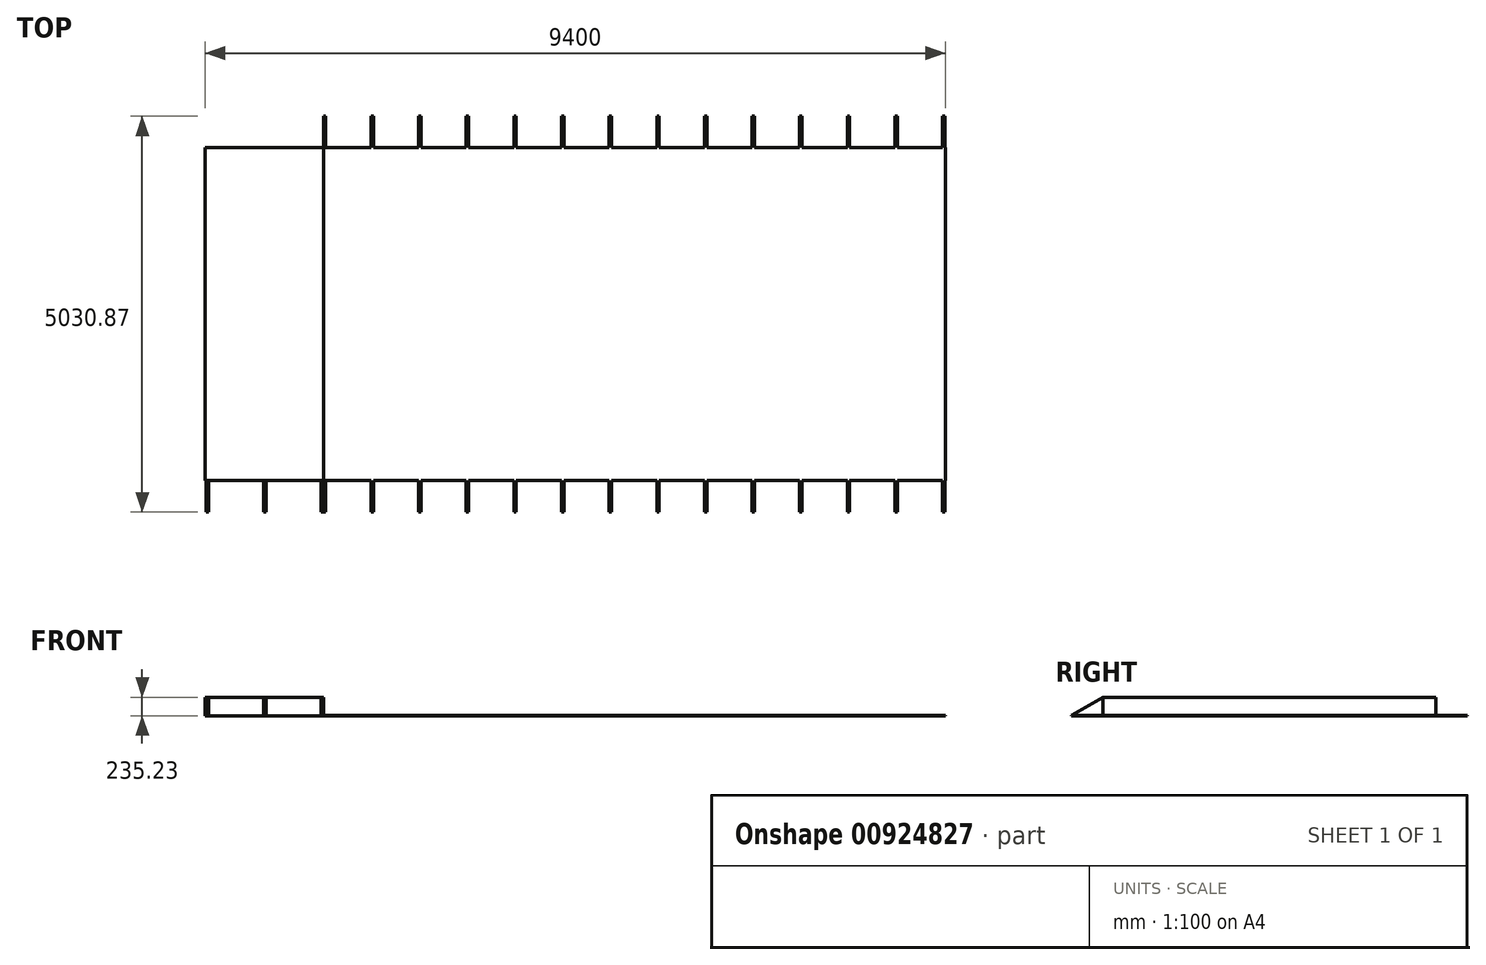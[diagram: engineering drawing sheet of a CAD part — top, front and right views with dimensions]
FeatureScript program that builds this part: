
annotation { "Feature Type Name" : "Feature", "Feature Type Description" : "" }
export const myFeature = defineFeature(function(context is Context, id is Id, definition is map)
    precondition{}
    {
        {
            var Q0;
            Q0=qCreatedBy(makeId("Top.planeOp"),FACE);
            var sketch = newSketch(context, id + "F0", { "sketchPlane" : qUnion([Q0])});
            skLineSegment(sketch, "E0.bottom", {"start": v(-1549.76, 3949.93) * mm, "end": v(-49.76, 3949.93) * mm});
            skLineSegment(sketch, "E0.top", {"start": v(-1549.76, -280.07) * mm, "end": v(-49.76, -280.07) * mm});
            skLineSegment(sketch, "E0.left", {"start": v(-1549.76, 3949.93) * mm, "end": v(-1549.76, -280.07) * mm});
            skLineSegment(sketch, "E0.right", {"start": v(-49.76, 3949.93) * mm, "end": v(-49.76, -280.07) * mm});
            skSolve(sketch);
        }
        {
            var Q0;
            Q0 = qSketchRegion(id + "F0", true);
            extrude(context, id + "F1", {"entities" : qUnion([Q0]), "depth" : 235 * mm, "offsetDistance" : 25 * mm});
        }
        {
            var Q0;
            Q0=qCreatedBy(makeId("Top.planeOp"),FACE);
            var sketch = newSketch(context, id + "F2", { "sketchPlane" : qUnion([Q0])});
            skLineSegment(sketch, "E1.bottom", {"start": v(-49.76, 3949.93) * mm, "end": v(7850.24, 3949.93) * mm});
            skLineSegment(sketch, "E1.top", {"start": v(-49.76, -280.07) * mm, "end": v(7850.24, -280.07) * mm});
            skLineSegment(sketch, "E1.left", {"start": v(-49.76, 3949.93) * mm, "end": v(-49.76, -280.07) * mm});
            skLineSegment(sketch, "E1.right", {"start": v(7850.24, 3949.93) * mm, "end": v(7850.24, -280.07) * mm});
            skSolve(sketch);
        }
        {
            var Q0;
            Q0 = qSketchRegion(id + "F2", true);
            extrude(context, id + "F3", {"entities" : qUnion([Q0]), "operationType" : NewBodyOperationType.ADD, "depth" : 2 * mm, "offsetDistance" : 25 * mm});
        }
        {
            var Q0;
            Q0=qCreatedBy(makeId("Top.planeOp"),FACE);
            var sketch = newSketch(context, id + "F4", { "sketchPlane" : qUnion([Q0])});
            skLineSegment(sketch, "E2.bottom", {"start": v(-49.76, 3949.93) * mm, "end": v(-19.76, 3949.93) * mm});
            skLineSegment(sketch, "E2.top", {"start": v(-49.76, 4349.93) * mm, "end": v(-19.76, 4349.93) * mm});
            skLineSegment(sketch, "E2.left", {"start": v(-49.76, 3949.93) * mm, "end": v(-49.76, 4349.93) * mm});
            skLineSegment(sketch, "E2.right", {"start": v(-19.76, 3949.93) * mm, "end": v(-19.76, 4349.93) * mm});
            skLineSegment(sketch, "E3", {"start": v(-2578.41, 1834.93) * mm, "end": v(9078.03, 1834.93) * mm, "construction": true});
            skLineSegment(sketch, "E4.1.0.0", {"start": v(585.24, 3949.93) * mm, "end": v(585.24, 4349.93) * mm});
            skLineSegment(sketch, "E4.1.0.1", {"start": v(555.24, 4349.93) * mm, "end": v(585.24, 4349.93) * mm});
            skLineSegment(sketch, "E4.1.0.2", {"start": v(555.24, 3949.93) * mm, "end": v(555.24, 4349.93) * mm});
            skLineSegment(sketch, "E4.1.0.3", {"start": v(555.24, 3949.93) * mm, "end": v(585.24, 3949.93) * mm});
            skLineSegment(sketch, "E4.2.0.0", {"start": v(1190.24, 3949.93) * mm, "end": v(1190.24, 4349.93) * mm});
            skLineSegment(sketch, "E4.2.0.1", {"start": v(1160.24, 4349.93) * mm, "end": v(1190.24, 4349.93) * mm});
            skLineSegment(sketch, "E4.2.0.2", {"start": v(1160.24, 3949.93) * mm, "end": v(1160.24, 4349.93) * mm});
            skLineSegment(sketch, "E4.2.0.3", {"start": v(1160.24, 3949.93) * mm, "end": v(1190.24, 3949.93) * mm});
            skLineSegment(sketch, "E4.3.0.0", {"start": v(1795.24, 3949.93) * mm, "end": v(1795.24, 4349.93) * mm});
            skLineSegment(sketch, "E4.3.0.1", {"start": v(1765.24, 4349.93) * mm, "end": v(1795.24, 4349.93) * mm});
            skLineSegment(sketch, "E4.3.0.2", {"start": v(1765.24, 3949.93) * mm, "end": v(1765.24, 4349.93) * mm});
            skLineSegment(sketch, "E4.3.0.3", {"start": v(1765.24, 3949.93) * mm, "end": v(1795.24, 3949.93) * mm});
            skLineSegment(sketch, "E4.4.0.0", {"start": v(2400.24, 3949.93) * mm, "end": v(2400.24, 4349.93) * mm});
            skLineSegment(sketch, "E4.4.0.1", {"start": v(2370.24, 4349.93) * mm, "end": v(2400.24, 4349.93) * mm});
            skLineSegment(sketch, "E4.4.0.2", {"start": v(2370.24, 3949.93) * mm, "end": v(2370.24, 4349.93) * mm});
            skLineSegment(sketch, "E4.4.0.3", {"start": v(2370.24, 3949.93) * mm, "end": v(2400.24, 3949.93) * mm});
            skLineSegment(sketch, "E4.5.0.0", {"start": v(3005.24, 3949.93) * mm, "end": v(3005.24, 4349.93) * mm});
            skLineSegment(sketch, "E4.5.0.1", {"start": v(2975.24, 4349.93) * mm, "end": v(3005.24, 4349.93) * mm});
            skLineSegment(sketch, "E4.5.0.2", {"start": v(2975.24, 3949.93) * mm, "end": v(2975.24, 4349.93) * mm});
            skLineSegment(sketch, "E4.5.0.3", {"start": v(2975.24, 3949.93) * mm, "end": v(3005.24, 3949.93) * mm});
            skLineSegment(sketch, "E4.6.0.0", {"start": v(3610.24, 3949.93) * mm, "end": v(3610.24, 4349.93) * mm});
            skLineSegment(sketch, "E4.6.0.1", {"start": v(3580.24, 4349.93) * mm, "end": v(3610.24, 4349.93) * mm});
            skLineSegment(sketch, "E4.6.0.2", {"start": v(3580.24, 3949.93) * mm, "end": v(3580.24, 4349.93) * mm});
            skLineSegment(sketch, "E4.6.0.3", {"start": v(3580.24, 3949.93) * mm, "end": v(3610.24, 3949.93) * mm});
            skLineSegment(sketch, "E4.7.0.0", {"start": v(4215.24, 3949.93) * mm, "end": v(4215.24, 4349.93) * mm});
            skLineSegment(sketch, "E4.7.0.1", {"start": v(4185.24, 4349.93) * mm, "end": v(4215.24, 4349.93) * mm});
            skLineSegment(sketch, "E4.7.0.2", {"start": v(4185.24, 3949.93) * mm, "end": v(4185.24, 4349.93) * mm});
            skLineSegment(sketch, "E4.7.0.3", {"start": v(4185.24, 3949.93) * mm, "end": v(4215.24, 3949.93) * mm});
            skLineSegment(sketch, "E4.8.0.0", {"start": v(4820.24, 3949.93) * mm, "end": v(4820.24, 4349.93) * mm});
            skLineSegment(sketch, "E4.8.0.1", {"start": v(4790.24, 4349.93) * mm, "end": v(4820.24, 4349.93) * mm});
            skLineSegment(sketch, "E4.8.0.2", {"start": v(4790.24, 3949.93) * mm, "end": v(4790.24, 4349.93) * mm});
            skLineSegment(sketch, "E4.8.0.3", {"start": v(4790.24, 3949.93) * mm, "end": v(4820.24, 3949.93) * mm});
            skLineSegment(sketch, "E4.9.0.0", {"start": v(5425.24, 3949.93) * mm, "end": v(5425.24, 4349.93) * mm});
            skLineSegment(sketch, "E4.9.0.1", {"start": v(5395.24, 4349.93) * mm, "end": v(5425.24, 4349.93) * mm});
            skLineSegment(sketch, "E4.9.0.2", {"start": v(5395.24, 3949.93) * mm, "end": v(5395.24, 4349.93) * mm});
            skLineSegment(sketch, "E4.9.0.3", {"start": v(5395.24, 3949.93) * mm, "end": v(5425.24, 3949.93) * mm});
            skLineSegment(sketch, "E4.10.0.0", {"start": v(6030.24, 3949.93) * mm, "end": v(6030.24, 4349.93) * mm});
            skLineSegment(sketch, "E4.10.0.1", {"start": v(6000.24, 4349.93) * mm, "end": v(6030.24, 4349.93) * mm});
            skLineSegment(sketch, "E4.10.0.2", {"start": v(6000.24, 3949.93) * mm, "end": v(6000.24, 4349.93) * mm});
            skLineSegment(sketch, "E4.10.0.3", {"start": v(6000.24, 3949.93) * mm, "end": v(6030.24, 3949.93) * mm});
            skLineSegment(sketch, "E4.11.0.0", {"start": v(6635.24, 3949.93) * mm, "end": v(6635.24, 4349.93) * mm});
            skLineSegment(sketch, "E4.11.0.1", {"start": v(6605.24, 4349.93) * mm, "end": v(6635.24, 4349.93) * mm});
            skLineSegment(sketch, "E4.11.0.2", {"start": v(6605.24, 3949.93) * mm, "end": v(6605.24, 4349.93) * mm});
            skLineSegment(sketch, "E4.11.0.3", {"start": v(6605.24, 3949.93) * mm, "end": v(6635.24, 3949.93) * mm});
            skLineSegment(sketch, "E4.12.0.0", {"start": v(7240.24, 3949.93) * mm, "end": v(7240.24, 4349.93) * mm});
            skLineSegment(sketch, "E4.12.0.1", {"start": v(7210.24, 4349.93) * mm, "end": v(7240.24, 4349.93) * mm});
            skLineSegment(sketch, "E4.12.0.2", {"start": v(7210.24, 3949.93) * mm, "end": v(7210.24, 4349.93) * mm});
            skLineSegment(sketch, "E4.12.0.3", {"start": v(7210.24, 3949.93) * mm, "end": v(7240.24, 3949.93) * mm});
            skLineSegment(sketch, "E4.13.0.0", {"start": v(7845.24, 3949.93) * mm, "end": v(7845.24, 4349.93) * mm});
            skLineSegment(sketch, "E4.13.0.1", {"start": v(7815.24, 4349.93) * mm, "end": v(7845.24, 4349.93) * mm});
            skLineSegment(sketch, "E4.13.0.2", {"start": v(7815.24, 3949.93) * mm, "end": v(7815.24, 4349.93) * mm});
            skLineSegment(sketch, "E4.13.0.3", {"start": v(7815.24, 3949.93) * mm, "end": v(7845.24, 3949.93) * mm});
            skLineSegment(sketch, "E4.direction1", {"start": v(-19.76, 3949.93) * mm, "end": v(585.24, 3949.93) * mm, "construction": true});
            skLineSegment(sketch, "E5.MirrorCS", {"start": v(-49.76, -680.07) * mm, "end": v(-19.76, -680.07) * mm});
            skLineSegment(sketch, "E6.MirrorCS", {"start": v(-19.76, -280.07) * mm, "end": v(-19.76, -680.07) * mm});
            skLineSegment(sketch, "E7.MirrorCS", {"start": v(-49.76, -280.07) * mm, "end": v(-49.76, -680.07) * mm});
            skLineSegment(sketch, "E8.MirrorCS", {"start": v(-49.76, -280.07) * mm, "end": v(-19.76, -280.07) * mm});
            skLineSegment(sketch, "E9.MirrorCS", {"start": v(555.24, -280.07) * mm, "end": v(585.24, -280.07) * mm});
            skLineSegment(sketch, "E10.MirrorCS", {"start": v(1765.24, -680.07) * mm, "end": v(1795.24, -680.07) * mm});
            skLineSegment(sketch, "E11.MirrorCS", {"start": v(7210.24, -280.07) * mm, "end": v(7240.24, -280.07) * mm});
            skLineSegment(sketch, "E12.MirrorCS", {"start": v(4790.24, -680.07) * mm, "end": v(4820.24, -680.07) * mm});
            skLineSegment(sketch, "E13.MirrorCS", {"start": v(3580.24, -280.07) * mm, "end": v(3610.24, -280.07) * mm});
            skLineSegment(sketch, "E14.MirrorCS", {"start": v(2370.24, -280.07) * mm, "end": v(2400.24, -280.07) * mm});
            skLineSegment(sketch, "E15.MirrorCS", {"start": v(5395.24, -280.07) * mm, "end": v(5425.24, -280.07) * mm});
            skLineSegment(sketch, "E16.MirrorCS", {"start": v(7815.24, -280.07) * mm, "end": v(7845.24, -280.07) * mm});
            skLineSegment(sketch, "E17.MirrorCS", {"start": v(6605.24, -280.07) * mm, "end": v(6635.24, -280.07) * mm});
            skLineSegment(sketch, "E18.MirrorCS", {"start": v(6000.24, -680.07) * mm, "end": v(6030.24, -680.07) * mm});
            skLineSegment(sketch, "E19.MirrorCS", {"start": v(555.24, -680.07) * mm, "end": v(585.24, -680.07) * mm});
            skLineSegment(sketch, "E20.MirrorCS", {"start": v(1765.24, -280.07) * mm, "end": v(1795.24, -280.07) * mm});
            skLineSegment(sketch, "E21.MirrorCS", {"start": v(2370.24, -680.07) * mm, "end": v(2400.24, -680.07) * mm});
            skLineSegment(sketch, "E22.MirrorCS", {"start": v(2975.24, -280.07) * mm, "end": v(3005.24, -280.07) * mm});
            skLineSegment(sketch, "E23.MirrorCS", {"start": v(7210.24, -680.07) * mm, "end": v(7240.24, -680.07) * mm});
            skLineSegment(sketch, "E24.MirrorCS", {"start": v(2975.24, -680.07) * mm, "end": v(3005.24, -680.07) * mm});
            skLineSegment(sketch, "E25.MirrorCS", {"start": v(4185.24, -680.07) * mm, "end": v(4215.24, -680.07) * mm});
            skLineSegment(sketch, "E26.MirrorCS", {"start": v(3580.24, -680.07) * mm, "end": v(3610.24, -680.07) * mm});
            skLineSegment(sketch, "E27.MirrorCS", {"start": v(7815.24, -680.07) * mm, "end": v(7845.24, -680.07) * mm});
            skLineSegment(sketch, "E28.MirrorCS", {"start": v(4790.24, -280.07) * mm, "end": v(4820.24, -280.07) * mm});
            skLineSegment(sketch, "E29.MirrorCS", {"start": v(4185.24, -280.07) * mm, "end": v(4215.24, -280.07) * mm});
            skLineSegment(sketch, "E30.MirrorCS", {"start": v(5395.24, -680.07) * mm, "end": v(5425.24, -680.07) * mm});
            skLineSegment(sketch, "E31.MirrorCS", {"start": v(6000.24, -280.07) * mm, "end": v(6030.24, -280.07) * mm});
            skLineSegment(sketch, "E32.MirrorCS", {"start": v(1160.24, -680.07) * mm, "end": v(1190.24, -680.07) * mm});
            skLineSegment(sketch, "E33.MirrorCS", {"start": v(1160.24, -280.07) * mm, "end": v(1190.24, -280.07) * mm});
            skLineSegment(sketch, "E34.MirrorCS", {"start": v(6605.24, -680.07) * mm, "end": v(6635.24, -680.07) * mm});
            skLineSegment(sketch, "E35.MirrorCS", {"start": v(585.24, -280.07) * mm, "end": v(585.24, -680.07) * mm});
            skLineSegment(sketch, "E36.MirrorCS", {"start": v(1795.24, -280.07) * mm, "end": v(1795.24, -680.07) * mm});
            skLineSegment(sketch, "E37.MirrorCS", {"start": v(6000.24, -280.07) * mm, "end": v(6000.24, -680.07) * mm});
            skLineSegment(sketch, "E38.MirrorCS", {"start": v(4790.24, -280.07) * mm, "end": v(4790.24, -680.07) * mm});
            skLineSegment(sketch, "E39.MirrorCS", {"start": v(4820.24, -280.07) * mm, "end": v(4820.24, -680.07) * mm});
            skLineSegment(sketch, "E40.MirrorCS", {"start": v(7210.24, -280.07) * mm, "end": v(7210.24, -680.07) * mm});
            skLineSegment(sketch, "E41.MirrorCS", {"start": v(3580.24, -280.07) * mm, "end": v(3580.24, -680.07) * mm});
            skLineSegment(sketch, "E42.MirrorCS", {"start": v(1765.24, -280.07) * mm, "end": v(1765.24, -680.07) * mm});
            skLineSegment(sketch, "E43.MirrorCS", {"start": v(555.24, -280.07) * mm, "end": v(555.24, -680.07) * mm});
            skLineSegment(sketch, "E44.MirrorCS", {"start": v(6605.24, -280.07) * mm, "end": v(6605.24, -680.07) * mm});
            skLineSegment(sketch, "E45.MirrorCS", {"start": v(1190.24, -280.07) * mm, "end": v(1190.24, -680.07) * mm});
            skLineSegment(sketch, "E46.MirrorCS", {"start": v(7240.24, -280.07) * mm, "end": v(7240.24, -680.07) * mm});
            skLineSegment(sketch, "E47.MirrorCS", {"start": v(4185.24, -280.07) * mm, "end": v(4185.24, -680.07) * mm});
            skLineSegment(sketch, "E48.MirrorCS", {"start": v(4215.24, -280.07) * mm, "end": v(4215.24, -680.07) * mm});
            skLineSegment(sketch, "E49.MirrorCS", {"start": v(7815.24, -280.07) * mm, "end": v(7815.24, -680.07) * mm});
            skLineSegment(sketch, "E50.MirrorCS", {"start": v(5425.24, -280.07) * mm, "end": v(5425.24, -680.07) * mm});
            skLineSegment(sketch, "E51.MirrorCS", {"start": v(6030.24, -280.07) * mm, "end": v(6030.24, -680.07) * mm});
            skLineSegment(sketch, "E52.MirrorCS", {"start": v(3610.24, -280.07) * mm, "end": v(3610.24, -680.07) * mm});
            skLineSegment(sketch, "E53.MirrorCS", {"start": v(5395.24, -280.07) * mm, "end": v(5395.24, -680.07) * mm});
            skLineSegment(sketch, "E54.MirrorCS", {"start": v(6635.24, -280.07) * mm, "end": v(6635.24, -680.07) * mm});
            skLineSegment(sketch, "E55.MirrorCS", {"start": v(2400.24, -280.07) * mm, "end": v(2400.24, -680.07) * mm});
            skLineSegment(sketch, "E56.MirrorCS", {"start": v(1160.24, -280.07) * mm, "end": v(1160.24, -680.07) * mm});
            skLineSegment(sketch, "E57.MirrorCS", {"start": v(2975.24, -280.07) * mm, "end": v(2975.24, -680.07) * mm});
            skLineSegment(sketch, "E58.MirrorCS", {"start": v(2370.24, -280.07) * mm, "end": v(2370.24, -680.07) * mm});
            skLineSegment(sketch, "E59.MirrorCS", {"start": v(7845.24, -280.07) * mm, "end": v(7845.24, -680.07) * mm});
            skLineSegment(sketch, "E60.MirrorCS", {"start": v(3005.24, -280.07) * mm, "end": v(3005.24, -680.07) * mm});
            skSolve(sketch);
        }
        {
            var Q0;
            Q0 = qSketchRegion(id + "F4", true);
            extrude(context, id + "F5", {"entities" : qUnion([Q0]), "operationType" : NewBodyOperationType.ADD, "depth" : 2 * mm, "offsetDistance" : 25 * mm});
        }
        {
            var Q0;
            Q0=makeQuery(id+"F1.opExtrude","CAP_VERTEX",VERTEX,{"disambiguationData":[OSD([sQuery(id+"F0.wireOp",EDGE,"E0.top"),sQuery(id+"F0.wireOp",EDGE,"E0.right")])],"isStart":false});
            var Q1;
            Q1=makeQuery(id+"F5.opExtrude","CAP_VERTEX",VERTEX,{"disambiguationData":[OSD([sQuery(id+"F4.wireOp",EDGE,"E5.MirrorCS"),sQuery(id+"F4.wireOp",EDGE,"E7.MirrorCS")])],"isStart":false});
            var Q2;
            Q2=makeQuery(id+"F5.opExtrude","CAP_VERTEX",VERTEX,{"disambiguationData":[OSD([sQuery(id+"F4.wireOp",EDGE,"E19.MirrorCS"),sQuery(id+"F4.wireOp",EDGE,"E43.MirrorCS")])],"isStart":false});
            cPlane(context, id + "F6", {"entities" : qUnion([Q0, Q1, Q2]), "cplaneType" : CPlaneType.THREE_POINT, "offset" : 25 * mm, "width" : 150 * mm, "height" : 150 * mm});
        }
        {
            var Q0;
            Q0=qCreatedBy(id+"F6.planeOp",FACE);
            var sketch = newSketch(context, id + "F7", { "sketchPlane" : qUnion([Q0])});
            skLineSegment(sketch, "E61", {"start": v(-49.76, 123.72) * mm, "end": v(-49.76, 587.65) * mm});
            skLineSegment(sketch, "E62", {"start": v(-49.76, 587.65) * mm, "end": v(-79.76, 587.65) * mm});
            skLineSegment(sketch, "E63", {"start": v(-79.76, 587.65) * mm, "end": v(-79.76, 123.72) * mm});
            skLineSegment(sketch, "E64", {"start": v(-79.76, 123.72) * mm, "end": v(-49.76, 123.72) * mm});
            skLineSegment(sketch, "E65.1.0.0", {"start": v(-809.76, 123.72) * mm, "end": v(-779.76, 123.72) * mm});
            skLineSegment(sketch, "E65.1.0.1", {"start": v(-809.76, 587.65) * mm, "end": v(-809.76, 123.72) * mm});
            skLineSegment(sketch, "E65.1.0.2", {"start": v(-779.76, 587.65) * mm, "end": v(-809.76, 587.65) * mm});
            skLineSegment(sketch, "E65.1.0.3", {"start": v(-779.76, 123.72) * mm, "end": v(-779.76, 587.65) * mm});
            skLineSegment(sketch, "E65.2.0.0", {"start": v(-1539.76, 123.72) * mm, "end": v(-1509.76, 123.72) * mm});
            skLineSegment(sketch, "E65.2.0.1", {"start": v(-1539.76, 587.65) * mm, "end": v(-1539.76, 123.72) * mm});
            skLineSegment(sketch, "E65.2.0.2", {"start": v(-1509.76, 587.65) * mm, "end": v(-1539.76, 587.65) * mm});
            skLineSegment(sketch, "E65.2.0.3", {"start": v(-1509.76, 123.72) * mm, "end": v(-1509.76, 587.65) * mm});
            skLineSegment(sketch, "E65.direction1", {"start": v(-79.76, 123.72) * mm, "end": v(-809.76, 123.72) * mm, "construction": true});
            skSolve(sketch);
        }
        {
            var Q0;
            Q0 = qSketchRegion(id + "F7", true);
            extrude(context, id + "F8", {"entities" : qUnion([Q0]), "operationType" : NewBodyOperationType.ADD, "depth" : 2 * mm, "offsetDistance" : 25 * mm});
        }
    });
